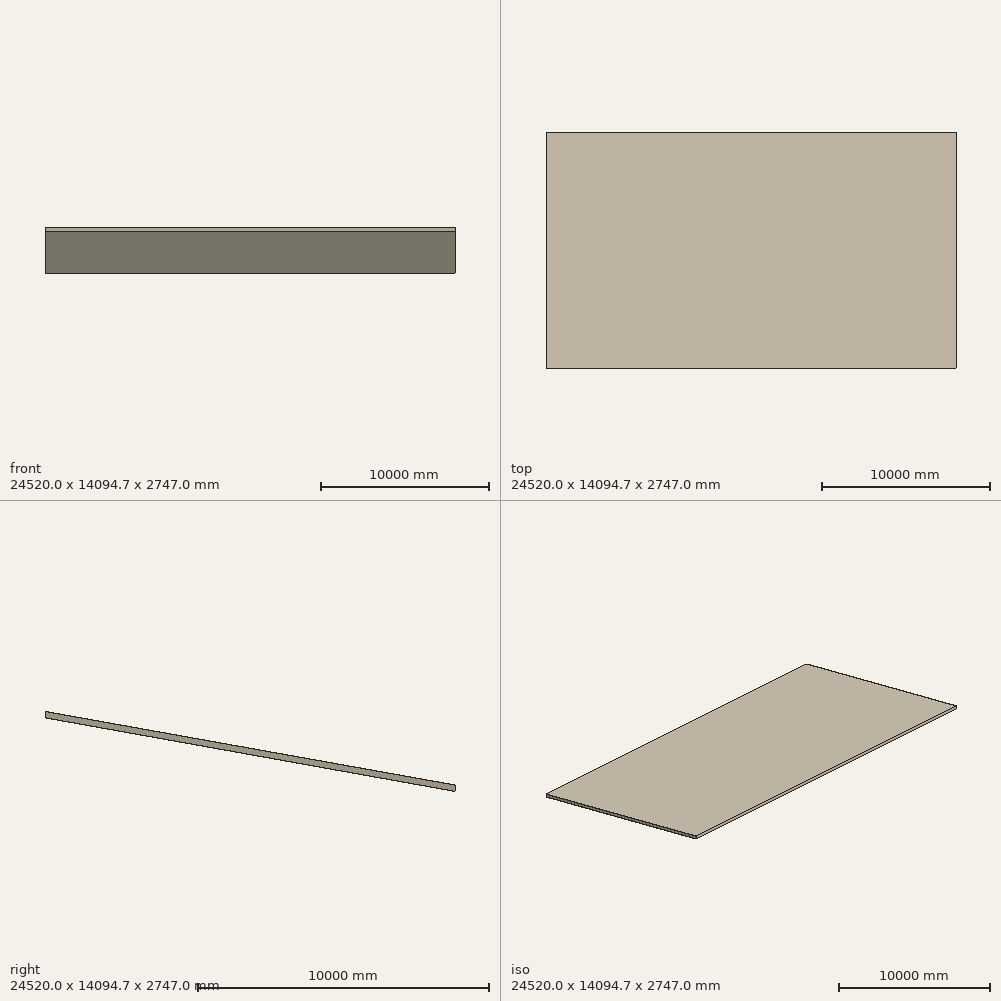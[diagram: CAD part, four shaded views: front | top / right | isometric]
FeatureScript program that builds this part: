
annotation { "Feature Type Name" : "Feature", "Feature Type Description" : "" }
export const myFeature = defineFeature(function(context is Context, id is Id, definition is map)
    precondition{}
    {
        {
            var Q0;
            Q0=qCreatedBy(makeId("Right.planeOp"),FACE);
            var sketch = newSketch(context, id + "F0", { "sketchPlane" : qUnion([Q0])});
            skLineSegment(sketch, "E0", {"start": v(0, 0) * mm, "end": v(0, 217) * mm});
            skLineSegment(sketch, "E1", {"start": v(0, 217) * mm, "end": v(14094.73, -2313) * mm});
            skLineSegment(sketch, "E2", {"start": v(14094.73, -2313) * mm, "end": v(14094.73, -2530) * mm});
            skLineSegment(sketch, "E3", {"start": v(14094.73, -2530) * mm, "end": v(0, 0) * mm});
            skSolve(sketch);
        }
        {
            var Q0;
            Q0 = qSketchRegion(id + "F0", true);
            extrude(context, id + "F1", {"entities" : qUnion([Q0]), "depth" : 24520 * mm});
        }
    });
